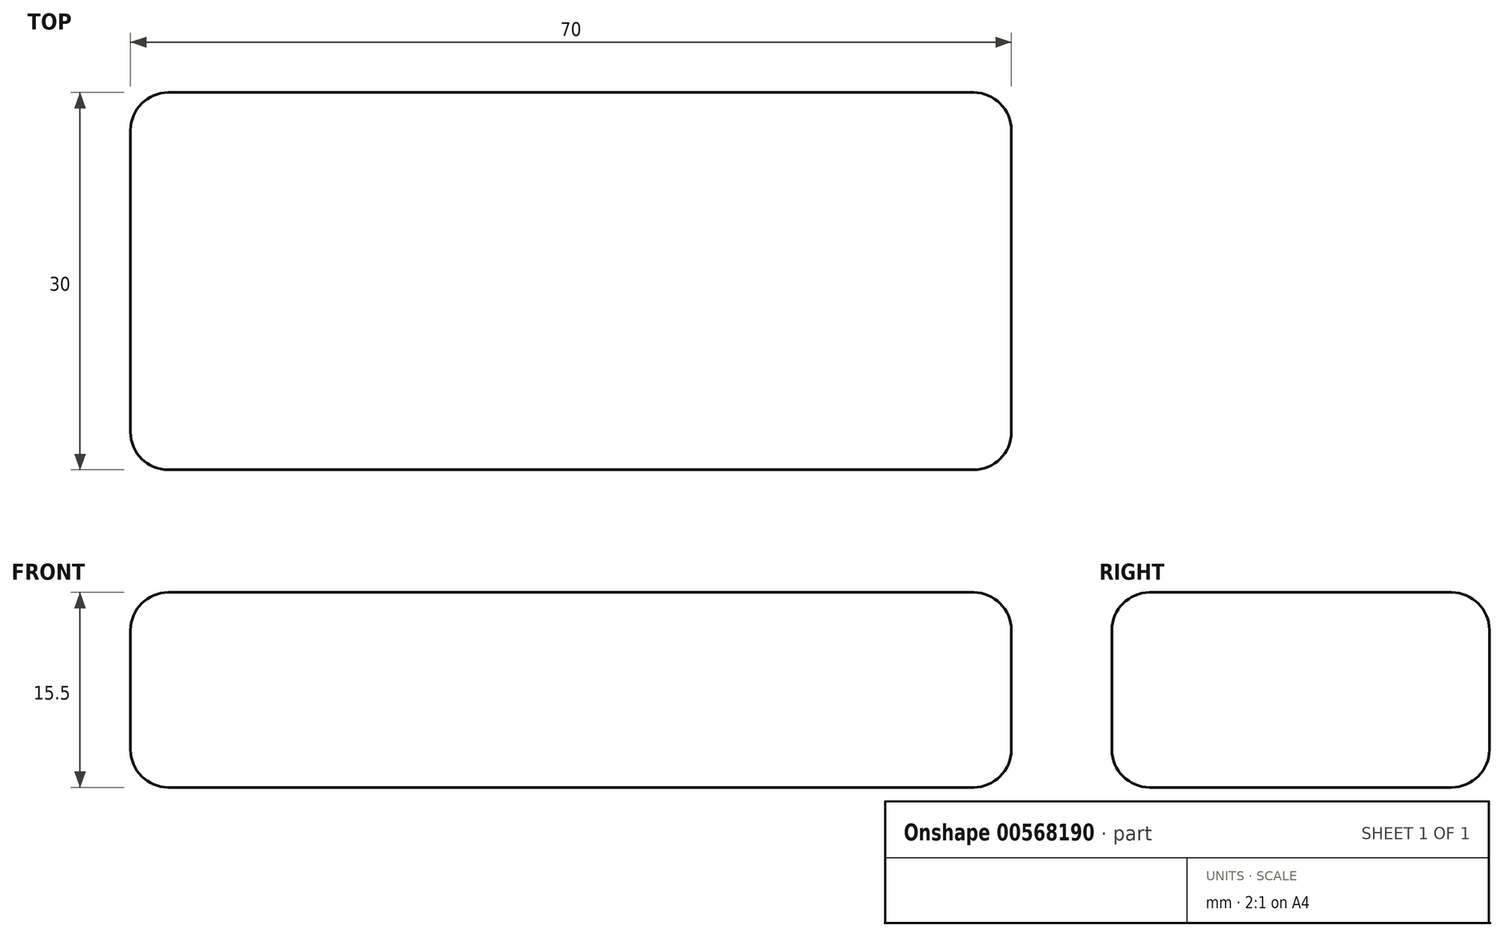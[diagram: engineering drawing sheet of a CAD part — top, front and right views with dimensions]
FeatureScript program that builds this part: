
annotation { "Feature Type Name" : "Feature", "Feature Type Description" : "" }
export const myFeature = defineFeature(function(context is Context, id is Id, definition is map)
    precondition{}
    {
        {
            var Q0;
            Q0=qCreatedBy(makeId("Top.planeOp"),FACE);
            var sketch = newSketch(context, id + "F0", { "sketchPlane" : qUnion([Q0])});
            skLineSegment(sketch, "E0.bottom", {"start": v(10.17, 0) * mm, "end": v(80.17, 0) * mm});
            skLineSegment(sketch, "E0.top", {"start": v(10.17, 30) * mm, "end": v(80.17, 30) * mm});
            skLineSegment(sketch, "E0.left", {"start": v(10.17, 0) * mm, "end": v(10.17, 30) * mm});
            skLineSegment(sketch, "E0.right", {"start": v(80.17, 0) * mm, "end": v(80.17, 30) * mm});
            skSolve(sketch);
        }
        {
            var Q0;
            Q0 = qSketchRegion(id + "F0", true);
            extrude(context, id + "F1", {"entities" : qUnion([Q0]), "depth" : 15.5 * mm, "offsetDistance" : 25 * mm});
        }
        {
            var Q0;
            Q0=makeQuery(id+"F1.opExtrude","SWEPT_EDGE",EDGE,{"disambiguationData":[OSD([sQuery(id+"F0.wireOp",EDGE,"E0.top"),sQuery(id+"F0.wireOp",EDGE,"E0.right")])]});
            var Q1;
            Q1=makeQuery(id+"F1.opExtrude","SWEPT_EDGE",EDGE,{"disambiguationData":[OSD([sQuery(id+"F0.wireOp",EDGE,"E0.bottom"),sQuery(id+"F0.wireOp",EDGE,"E0.right")])]});
            var Q2;
            Q2=makeQuery(id+"F1.opExtrude","CAP_EDGE",EDGE,{"disambiguationData":[OSD([sQuery(id+"F0.wireOp",EDGE,"E0.bottom")])],"isStart":true});
            var Q3;
            Q3=makeQuery(id+"F1.opExtrude","CAP_EDGE",EDGE,{"disambiguationData":[OSD([sQuery(id+"F0.wireOp",EDGE,"E0.bottom")])],"isStart":false});
            var Q4;
            Q4=makeQuery(id+"F1.opExtrude","CAP_EDGE",EDGE,{"disambiguationData":[OSD([sQuery(id+"F0.wireOp",EDGE,"E0.right")])],"isStart":true});
            var Q5;
            Q5=makeQuery(id+"F1.opExtrude","CAP_EDGE",EDGE,{"disambiguationData":[OSD([sQuery(id+"F0.wireOp",EDGE,"E0.right")])],"isStart":false});
            var Q6;
            Q6=makeQuery(id+"F1.opExtrude","SWEPT_EDGE",EDGE,{"disambiguationData":[OSD([sQuery(id+"F0.wireOp",EDGE,"E0.top"),sQuery(id+"F0.wireOp",EDGE,"E0.left")])]});
            var Q7;
            Q7=makeQuery(id+"F1.opExtrude","SWEPT_EDGE",EDGE,{"disambiguationData":[OSD([sQuery(id+"F0.wireOp",EDGE,"E0.bottom"),sQuery(id+"F0.wireOp",EDGE,"E0.left")])]});
            var Q8;
            Q8=makeQuery(id+"F1.opExtrude","CAP_EDGE",EDGE,{"disambiguationData":[OSD([sQuery(id+"F0.wireOp",EDGE,"E0.top")])],"isStart":true});
            var Q9;
            Q9=makeQuery(id+"F1.opExtrude","CAP_EDGE",EDGE,{"disambiguationData":[OSD([sQuery(id+"F0.wireOp",EDGE,"E0.top")])],"isStart":false});
            var Q10;
            Q10=makeQuery(id+"F1.opExtrude","CAP_EDGE",EDGE,{"disambiguationData":[OSD([sQuery(id+"F0.wireOp",EDGE,"E0.left")])],"isStart":true});
            var Q11;
            Q11=makeQuery(id+"F1.opExtrude","CAP_EDGE",EDGE,{"disambiguationData":[OSD([sQuery(id+"F0.wireOp",EDGE,"E0.left")])],"isStart":false});
            fillet(context, id + "F2", {"entities" : qUnion([Q0, Q1, Q2, Q3, Q4, Q5, Q6, Q7, Q8, Q9, Q10, Q11]), "radius" : 3 * mm, "tangentPropagation" : true, "allowEdgeOverflow" : false});
        }
    });
